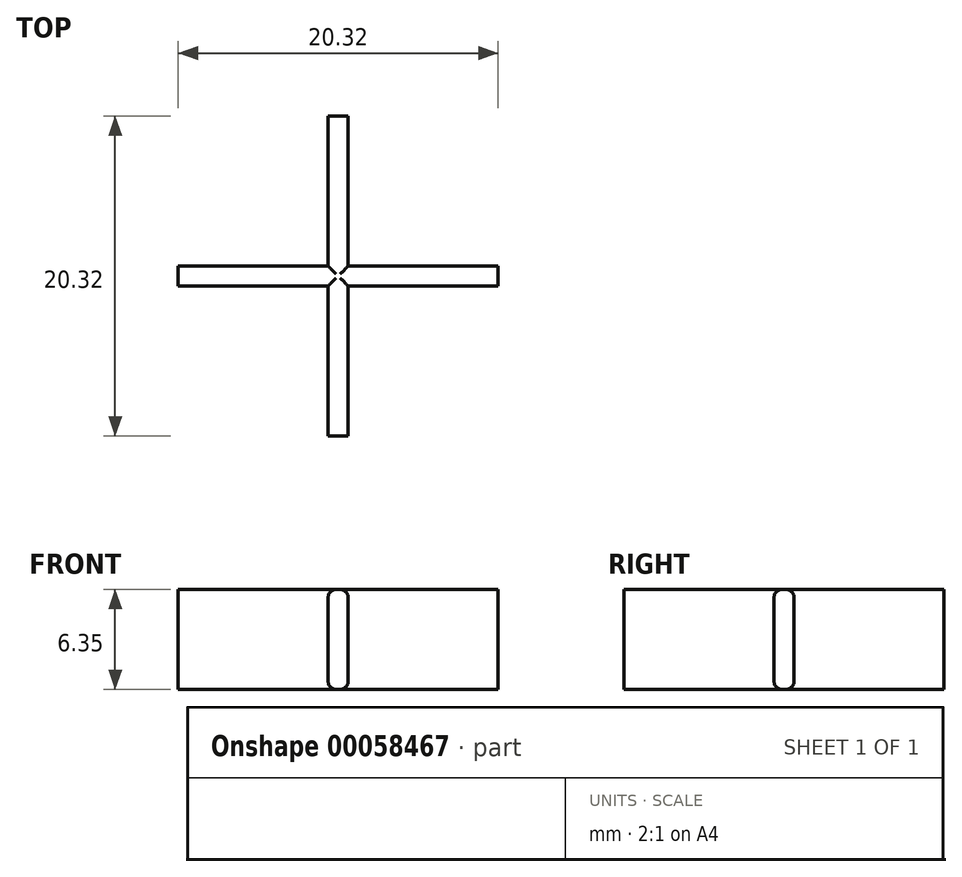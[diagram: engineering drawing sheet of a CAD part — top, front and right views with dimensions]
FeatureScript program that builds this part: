
annotation { "Feature Type Name" : "Feature", "Feature Type Description" : "" }
export const myFeature = defineFeature(function(context is Context, id is Id, definition is map)
    precondition{}
    {
        {
            var Q0;
            Q0=qCreatedBy(makeId("Top.planeOp"),FACE);
            var sketch = newSketch(context, id + "F0", { "sketchPlane" : qUnion([Q0])});
            skLineSegment(sketch, "E0.rect.bottom", {"start": v(10.16, 0.64) * mm, "end": v(-10.16, 0.64) * mm});
            skLineSegment(sketch, "E0.rect.top", {"start": v(10.16, -0.64) * mm, "end": v(-10.16, -0.64) * mm});
            skLineSegment(sketch, "E0.rect.left", {"start": v(10.16, 0.64) * mm, "end": v(10.16, -0.64) * mm});
            skLineSegment(sketch, "E0.rect.right", {"start": v(-10.16, 0.64) * mm, "end": v(-10.16, -0.64) * mm});
            skPoint(sketch, "E0.rect.middle", {"position": v(0, 0) * mm});
            skLineSegment(sketch, "E1.rect.bottom", {"start": v(0.63, 10.16) * mm, "end": v(-0.64, 10.16) * mm});
            skLineSegment(sketch, "E1.rect.top", {"start": v(0.64, -10.16) * mm, "end": v(-0.64, -10.16) * mm});
            skLineSegment(sketch, "E1.rect.left", {"start": v(0.63, 10.16) * mm, "end": v(0.64, -10.16) * mm});
            skLineSegment(sketch, "E1.rect.right", {"start": v(-0.64, 10.16) * mm, "end": v(-0.64, -10.16) * mm});
            skSolve(sketch);
        }
        {
            var Q0;
            {var subQ0=sQuery(id+"F0.wireOp",EDGE,"E0.rect.right");Q0=makeQuery(id+"F0.imprint","IMPRINT",FACE,{"disambiguationData":[TD([[makeQuery(id+"F0.imprint","IMPRINT",EDGE,{"derivedFrom":subQ0}),1.0]])]});}
            var Q1;
            {var subQ5=sQuery(id+"F0.wireOp",EDGE,"E1.rect.bottom");Q1=makeQuery(id+"F0.imprint","IMPRINT",FACE,{"disambiguationData":[TD([[makeQuery(id+"F0.imprint","IMPRINT",EDGE,{"derivedFrom":subQ5}),1.0]])]});}
            var Q2;
            {var subQ0=sQuery(id+"F0.wireOp",EDGE,"E0.rect.left");Q2=makeQuery(id+"F0.imprint","IMPRINT",FACE,{"disambiguationData":[TD([[makeQuery(id+"F0.imprint","IMPRINT",EDGE,{"derivedFrom":subQ0}),-1.0]])]});}
            var Q3;
            {var subQ5=sQuery(id+"F0.wireOp",EDGE,"E1.rect.top");Q3=makeQuery(id+"F0.imprint","IMPRINT",FACE,{"disambiguationData":[TD([[makeQuery(id+"F0.imprint","IMPRINT",EDGE,{"derivedFrom":subQ5}),-1.0]])]});}
            var Q4;
            {var subQ0=sQuery(id+"F0.wireOp",EDGE,"E1.rect.left");var subQ1=sQuery(id+"F0.wireOp",EDGE,"E0.rect.bottom");var subQ2=makeQuery(id+"F0.imprint","INTERSECT",VERTEX,{"derivedFrom":[subQ1,subQ0]});Q4=makeQuery(id+"F0.imprint","IMPRINT",FACE,{"disambiguationData":[TD([[makeQuery(id+"F0.imprint","IMPRINT",EDGE,{"disambiguationData":[TD([[subQ2,-1.0]])],"derivedFrom":subQ1}),1.0]])]});}
            extrude(context, id + "F1", {"entities" : qUnion([Q0, Q1, Q2, Q3, Q4]), "depth" : 6.35 * mm});
        }
        {
            var Q0;
            {var subQ0=sQuery(id+"F0.wireOp",EDGE,"E1.rect.left");Q0=makeQuery(id+"F1.opExtrude","CAP_EDGE",EDGE,{"disambiguationData":[OSD([subQ0]),TDD([makeQuery(id+"F0.imprint","IMPRINT",EDGE,{"disambiguationData":[TD([[makeQuery(id+"F0.imprint","INTERSECT",VERTEX,{"derivedFrom":[sQuery(id+"F0.wireOp",EDGE,"E1.rect.top"),subQ0]}),1.0]])],"derivedFrom":subQ0})])],"isStart":false});}
            var Q1;
            {var subQ0=sQuery(id+"F0.wireOp",EDGE,"E1.rect.right");Q1=makeQuery(id+"F1.opExtrude","CAP_EDGE",EDGE,{"disambiguationData":[OSD([subQ0]),TDD([makeQuery(id+"F0.imprint","IMPRINT",EDGE,{"disambiguationData":[TD([[makeQuery(id+"F0.imprint","INTERSECT",VERTEX,{"derivedFrom":[sQuery(id+"F0.wireOp",EDGE,"E1.rect.top"),subQ0]}),1.0]])],"derivedFrom":subQ0})])],"isStart":false});}
            var Q2;
            {var subQ0=sQuery(id+"F0.wireOp",EDGE,"E0.rect.top");Q2=makeQuery(id+"F1.opExtrude","CAP_EDGE",EDGE,{"disambiguationData":[OSD([subQ0]),TDD([makeQuery(id+"F0.imprint","IMPRINT",EDGE,{"disambiguationData":[TD([[makeQuery(id+"F0.imprint","INTERSECT",VERTEX,{"derivedFrom":[subQ0,sQuery(id+"F0.wireOp",EDGE,"E0.rect.right")]}),1.0]])],"derivedFrom":subQ0})])],"isStart":false});}
            var Q3;
            {var subQ0=sQuery(id+"F0.wireOp",EDGE,"E0.rect.bottom");Q3=makeQuery(id+"F1.opExtrude","CAP_EDGE",EDGE,{"disambiguationData":[OSD([subQ0]),TDD([makeQuery(id+"F0.imprint","IMPRINT",EDGE,{"disambiguationData":[TD([[makeQuery(id+"F0.imprint","INTERSECT",VERTEX,{"derivedFrom":[subQ0,sQuery(id+"F0.wireOp",EDGE,"E0.rect.right")]}),1.0]])],"derivedFrom":subQ0})])],"isStart":false});}
            var Q4;
            {var subQ0=sQuery(id+"F0.wireOp",EDGE,"E1.rect.right");Q4=makeQuery(id+"F1.opExtrude","CAP_EDGE",EDGE,{"disambiguationData":[OSD([subQ0]),TDD([makeQuery(id+"F0.imprint","IMPRINT",EDGE,{"disambiguationData":[TD([[makeQuery(id+"F0.imprint","INTERSECT",VERTEX,{"derivedFrom":[sQuery(id+"F0.wireOp",EDGE,"E1.rect.bottom"),subQ0]}),-1.0]])],"derivedFrom":subQ0})])],"isStart":false});}
            var Q5;
            {var subQ0=sQuery(id+"F0.wireOp",EDGE,"E1.rect.left");Q5=makeQuery(id+"F1.opExtrude","CAP_EDGE",EDGE,{"disambiguationData":[OSD([subQ0]),TDD([makeQuery(id+"F0.imprint","IMPRINT",EDGE,{"disambiguationData":[TD([[makeQuery(id+"F0.imprint","INTERSECT",VERTEX,{"derivedFrom":[sQuery(id+"F0.wireOp",EDGE,"E1.rect.bottom"),subQ0]}),-1.0]])],"derivedFrom":subQ0})])],"isStart":false});}
            var Q6;
            {var subQ0=sQuery(id+"F0.wireOp",EDGE,"E0.rect.bottom");Q6=makeQuery(id+"F1.opExtrude","CAP_EDGE",EDGE,{"disambiguationData":[OSD([subQ0]),TDD([makeQuery(id+"F0.imprint","IMPRINT",EDGE,{"disambiguationData":[TD([[makeQuery(id+"F0.imprint","INTERSECT",VERTEX,{"derivedFrom":[subQ0,sQuery(id+"F0.wireOp",EDGE,"E0.rect.left")]}),-1.0]])],"derivedFrom":subQ0})])],"isStart":false});}
            var Q7;
            {var subQ0=sQuery(id+"F0.wireOp",EDGE,"E0.rect.top");Q7=makeQuery(id+"F1.opExtrude","CAP_EDGE",EDGE,{"disambiguationData":[OSD([subQ0]),TDD([makeQuery(id+"F0.imprint","IMPRINT",EDGE,{"disambiguationData":[TD([[makeQuery(id+"F0.imprint","INTERSECT",VERTEX,{"derivedFrom":[subQ0,sQuery(id+"F0.wireOp",EDGE,"E0.rect.left")]}),-1.0]])],"derivedFrom":subQ0})])],"isStart":false});}
            var Q8;
            {var subQ0=sQuery(id+"F0.wireOp",EDGE,"E0.rect.bottom");Q8=makeQuery(id+"F1.opExtrude","CAP_EDGE",EDGE,{"disambiguationData":[OSD([subQ0]),TDD([makeQuery(id+"F0.imprint","IMPRINT",EDGE,{"disambiguationData":[TD([[makeQuery(id+"F0.imprint","INTERSECT",VERTEX,{"derivedFrom":[subQ0,sQuery(id+"F0.wireOp",EDGE,"E0.rect.right")]}),1.0]])],"derivedFrom":subQ0})])],"isStart":true});}
            var Q9;
            {var subQ0=sQuery(id+"F0.wireOp",EDGE,"E0.rect.top");Q9=makeQuery(id+"F1.opExtrude","CAP_EDGE",EDGE,{"disambiguationData":[OSD([subQ0]),TDD([makeQuery(id+"F0.imprint","IMPRINT",EDGE,{"disambiguationData":[TD([[makeQuery(id+"F0.imprint","INTERSECT",VERTEX,{"derivedFrom":[subQ0,sQuery(id+"F0.wireOp",EDGE,"E0.rect.right")]}),1.0]])],"derivedFrom":subQ0})])],"isStart":true});}
            var Q10;
            {var subQ0=sQuery(id+"F0.wireOp",EDGE,"E0.rect.top");Q10=makeQuery(id+"F1.opExtrude","CAP_EDGE",EDGE,{"disambiguationData":[OSD([subQ0]),TDD([makeQuery(id+"F0.imprint","IMPRINT",EDGE,{"disambiguationData":[TD([[makeQuery(id+"F0.imprint","INTERSECT",VERTEX,{"derivedFrom":[subQ0,sQuery(id+"F0.wireOp",EDGE,"E0.rect.left")]}),-1.0]])],"derivedFrom":subQ0})])],"isStart":true});}
            var Q11;
            {var subQ0=sQuery(id+"F0.wireOp",EDGE,"E0.rect.bottom");Q11=makeQuery(id+"F1.opExtrude","CAP_EDGE",EDGE,{"disambiguationData":[OSD([subQ0]),TDD([makeQuery(id+"F0.imprint","IMPRINT",EDGE,{"disambiguationData":[TD([[makeQuery(id+"F0.imprint","INTERSECT",VERTEX,{"derivedFrom":[subQ0,sQuery(id+"F0.wireOp",EDGE,"E0.rect.left")]}),-1.0]])],"derivedFrom":subQ0})])],"isStart":true});}
            var Q12;
            {var subQ0=sQuery(id+"F0.wireOp",EDGE,"E1.rect.left");Q12=makeQuery(id+"F1.opExtrude","CAP_EDGE",EDGE,{"disambiguationData":[OSD([subQ0]),TDD([makeQuery(id+"F0.imprint","IMPRINT",EDGE,{"disambiguationData":[TD([[makeQuery(id+"F0.imprint","INTERSECT",VERTEX,{"derivedFrom":[sQuery(id+"F0.wireOp",EDGE,"E1.rect.bottom"),subQ0]}),-1.0]])],"derivedFrom":subQ0})])],"isStart":true});}
            var Q13;
            {var subQ0=sQuery(id+"F0.wireOp",EDGE,"E1.rect.right");Q13=makeQuery(id+"F1.opExtrude","CAP_EDGE",EDGE,{"disambiguationData":[OSD([subQ0]),TDD([makeQuery(id+"F0.imprint","IMPRINT",EDGE,{"disambiguationData":[TD([[makeQuery(id+"F0.imprint","INTERSECT",VERTEX,{"derivedFrom":[sQuery(id+"F0.wireOp",EDGE,"E1.rect.bottom"),subQ0]}),-1.0]])],"derivedFrom":subQ0})])],"isStart":true});}
            var Q14;
            {var subQ0=sQuery(id+"F0.wireOp",EDGE,"E1.rect.right");Q14=makeQuery(id+"F1.opExtrude","CAP_EDGE",EDGE,{"disambiguationData":[OSD([subQ0]),TDD([makeQuery(id+"F0.imprint","IMPRINT",EDGE,{"disambiguationData":[TD([[makeQuery(id+"F0.imprint","INTERSECT",VERTEX,{"derivedFrom":[sQuery(id+"F0.wireOp",EDGE,"E1.rect.top"),subQ0]}),1.0]])],"derivedFrom":subQ0})])],"isStart":true});}
            var Q15;
            {var subQ0=sQuery(id+"F0.wireOp",EDGE,"E1.rect.left");Q15=makeQuery(id+"F1.opExtrude","CAP_EDGE",EDGE,{"disambiguationData":[OSD([subQ0]),TDD([makeQuery(id+"F0.imprint","IMPRINT",EDGE,{"disambiguationData":[TD([[makeQuery(id+"F0.imprint","INTERSECT",VERTEX,{"derivedFrom":[sQuery(id+"F0.wireOp",EDGE,"E1.rect.top"),subQ0]}),1.0]])],"derivedFrom":subQ0})])],"isStart":true});}
            fillet(context, id + "F2", {"entities" : qUnion([Q0, Q1, Q2, Q3, Q4, Q5, Q6, Q7, Q8, Q9, Q10, Q11, Q12, Q13, Q14, Q15]), "radius" : 0.5 * mm, "tangentPropagation" : true, "allowEdgeOverflow" : false});
        }
    });
